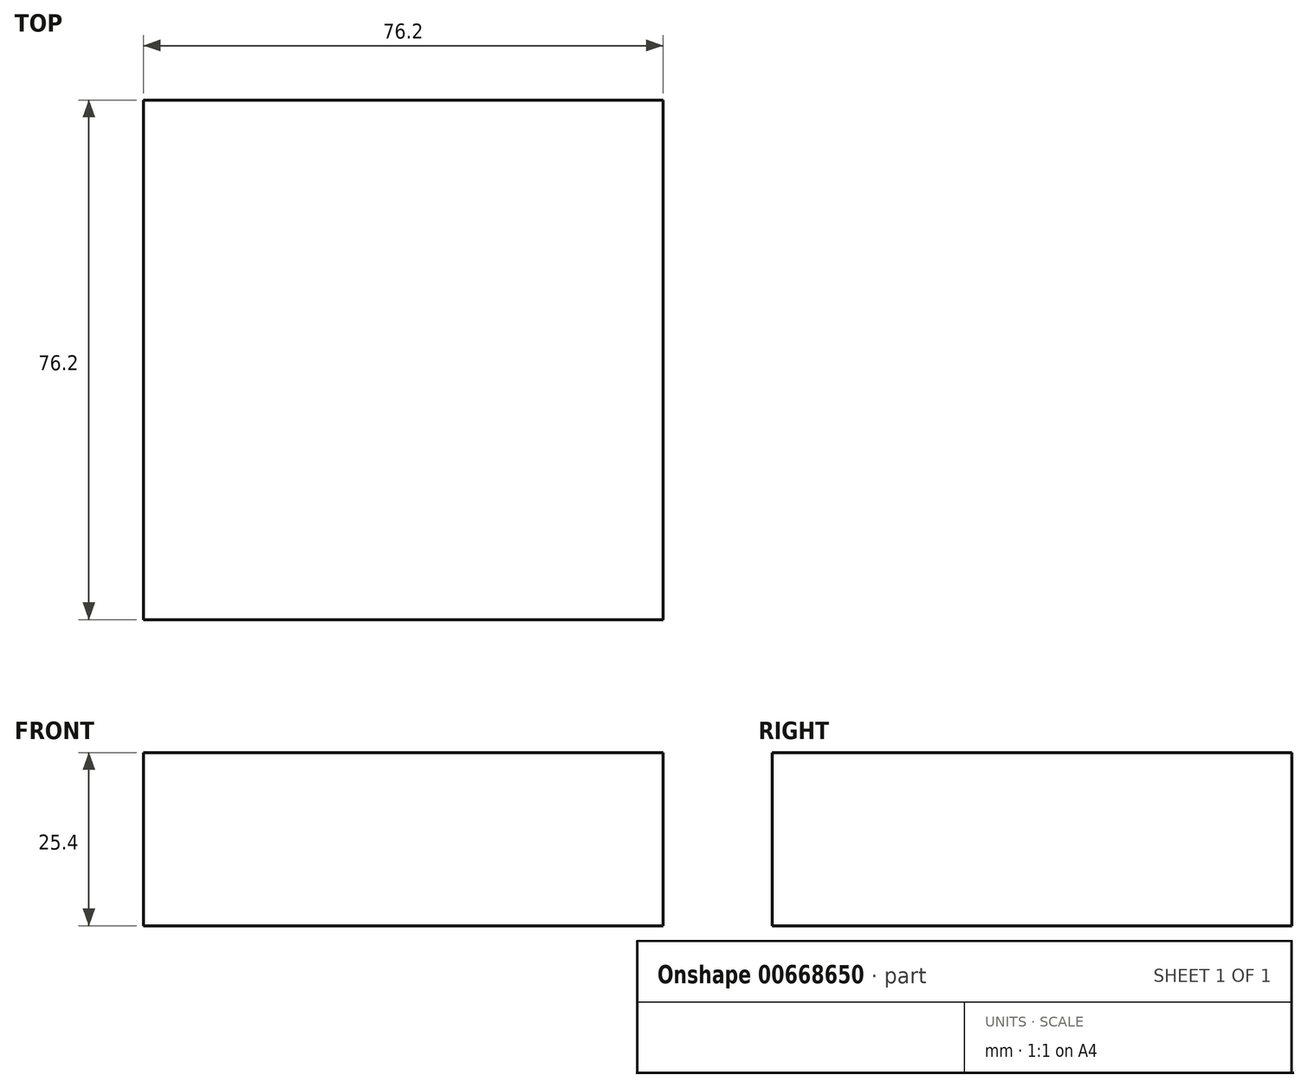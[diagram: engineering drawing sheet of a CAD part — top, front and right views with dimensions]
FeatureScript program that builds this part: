
annotation { "Feature Type Name" : "Feature", "Feature Type Description" : "" }
export const myFeature = defineFeature(function(context is Context, id is Id, definition is map)
    precondition{}
    {
        {
            var Q0;
            Q0=qCreatedBy(makeId("Top.planeOp"),FACE);
            var sketch = newSketch(context, id + "F0", { "sketchPlane" : qUnion([Q0])});
            skLineSegment(sketch, "E0", {"start": v(-35.52, 60.1) * mm, "end": v(40.68, 60.1) * mm});
            skLineSegment(sketch, "E1", {"start": v(40.68, 60.1) * mm, "end": v(40.68, -16.1) * mm});
            skLineSegment(sketch, "E2", {"start": v(40.68, -16.1) * mm, "end": v(-35.52, -16.1) * mm});
            skLineSegment(sketch, "E3", {"start": v(-35.52, -16.1) * mm, "end": v(-35.52, 60.1) * mm});
            skSolve(sketch);
        }
        {
            var Q0;
            Q0=makeQuery(id+"F0.imprint","IMPRINT",FACE,{"disambiguationData":[TD([[makeQuery(id+"F0.imprint","IMPRINT",EDGE,{"derivedFrom":sQuery(id+"F0.wireOp",EDGE,"E0")}),-1.0]])]});
            extrude(context, id + "F1", {"entities" : qUnion([Q0]), "depth" : 25.4 * mm, "offsetDistance" : 25.4 * mm});
        }
    });
